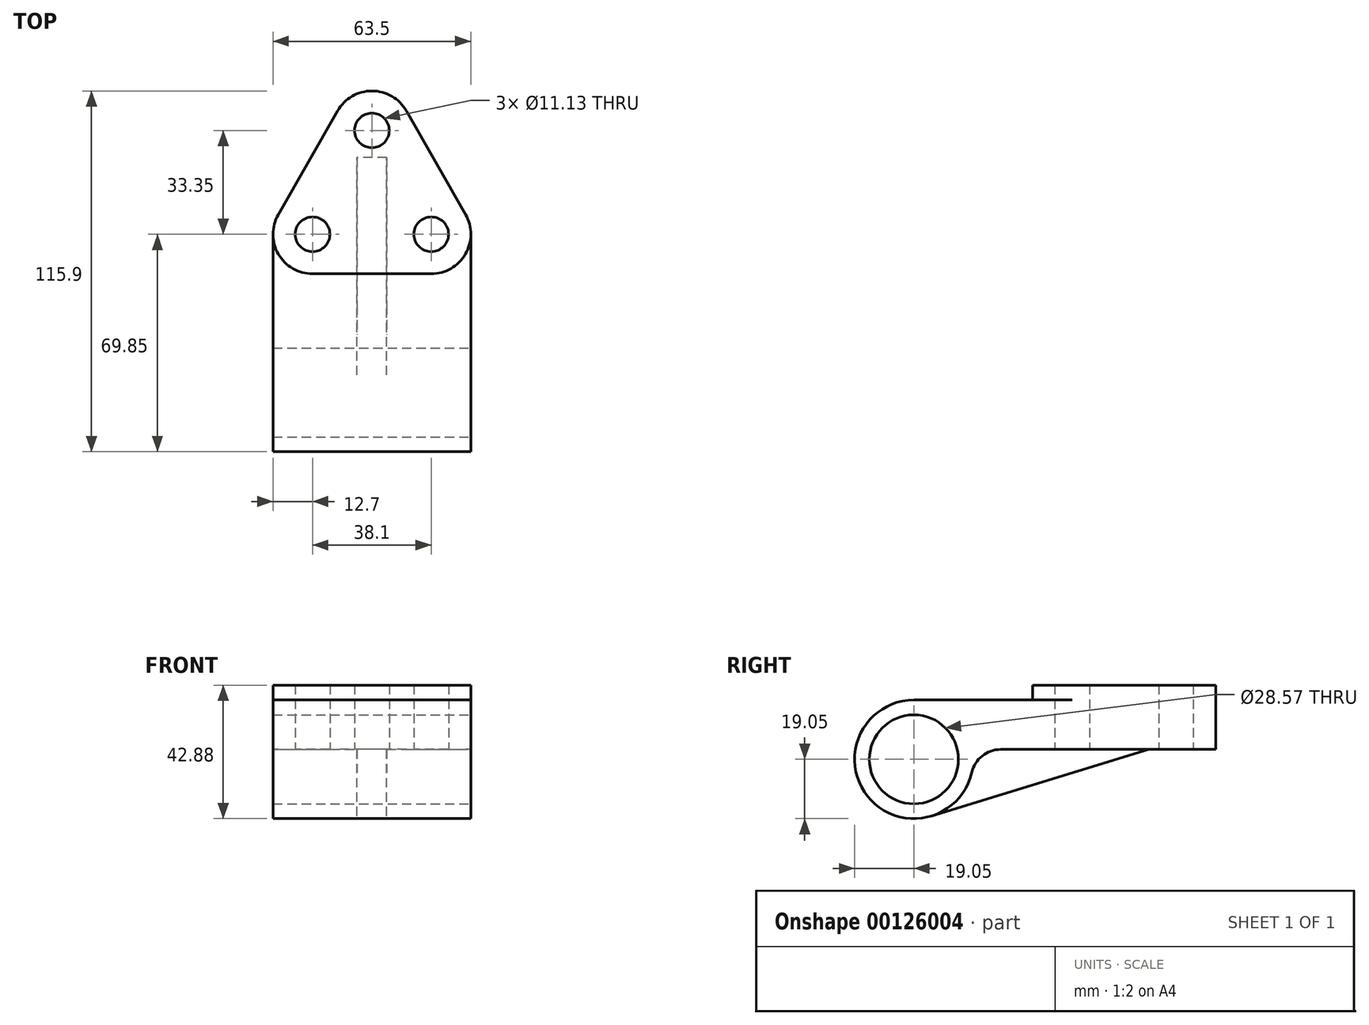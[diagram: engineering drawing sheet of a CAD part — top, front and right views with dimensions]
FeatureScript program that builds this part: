
annotation { "Feature Type Name" : "Feature", "Feature Type Description" : "" }
export const myFeature = defineFeature(function(context is Context, id is Id, definition is map)
    precondition{}
    {
        {
            var Q0;
            Q0=qCreatedBy(makeId("Right.planeOp"),FACE);
            var sketch = newSketch(context, id + "F0", { "sketchPlane" : qUnion([Q0])});
            skArc(sketch, "E0", {"start": v(0, 19.05) * mm, "mid": v(-12.3, -14.55) * mm, "end": v(18.78, 3.17) * mm});
            skCircle(sketch, "E1", {"center": v(0, 0) * mm, "radius": 14.29 * mm});
            skLineSegment(sketch, "E2", {"start": v(0, 19.05) * mm, "end": v(50.8, 19.05) * mm});
            skLineSegment(sketch, "E3", {"start": v(50.8, 19.05) * mm, "end": v(50.8, 3.17) * mm});
            skLineSegment(sketch, "E4", {"start": v(50.8, 3.17) * mm, "end": v(18.78, 3.17) * mm});
            skSolve(sketch);
        }
        {
            var Q0;
            Q0 = qSketchRegion(id + "F0", true);
            extrude(context, id + "F1", {"entities" : qUnion([Q0]), "endBound" : BoundingType.SYMMETRIC, "oppositeDirection" : true, "depth" : 63.5 * mm});
        }
        {
            var Q0;
            Q0=makeQuery(id+"F1.opExtrude","SWEPT_FACE",FACE,{"disambiguationData":[OSD([sQuery(id+"F0.wireOp",EDGE,"E2")])]});
            var sketch = newSketch(context, id + "F2", { "sketchPlane" : qUnion([Q0])});
            skLineSegment(sketch, "E5", {"start": v(0, 50.8) * mm, "end": v(19.05, 50.8) * mm, "construction": true});
            skLineSegment(sketch, "E6", {"start": v(0, 50.8) * mm, "end": v(-19.05, 50.8) * mm, "construction": true});
            skCircle(sketch, "E7", {"center": v(-19.05, 50.8) * mm, "radius": 5.56 * mm});
            skCircle(sketch, "E8", {"center": v(19.05, 50.8) * mm, "radius": 5.56 * mm});
            skArc(sketch, "E9", {"start": v(19.05, 38.1) * mm, "mid": v(30.03, 44.42) * mm, "end": v(30.08, 57.1) * mm});
            skArc(sketch, "E10", {"start": v(-30.08, 57.1) * mm, "mid": v(-30.03, 44.42) * mm, "end": v(-19.05, 38.1) * mm});
            skLineSegment(sketch, "E11", {"start": v(0, 50.8) * mm, "end": v(0, 84.15) * mm, "construction": true});
            skCircle(sketch, "E12", {"center": v(0, 84.15) * mm, "radius": 5.56 * mm});
            skArc(sketch, "E13", {"start": v(11.03, 90.45) * mm, "mid": v(0, 96.85) * mm, "end": v(-11.03, 90.45) * mm});
            skLineSegment(sketch, "E14", {"start": v(-19.05, 38.1) * mm, "end": v(19.05, 38.1) * mm});
            skLineSegment(sketch, "E15", {"start": v(-30.08, 57.1) * mm, "end": v(-11.03, 90.45) * mm});
            skLineSegment(sketch, "E16", {"start": v(11.03, 90.45) * mm, "end": v(30.08, 57.1) * mm});
            skSolve(sketch);
        }
        {
            var Q0;
            Q0 = qSketchRegion(id + "F2", true);
            var Q1;
            Q1=makeQuery(id+"F1.opExtrude","SWEPT_FACE",FACE,{"disambiguationData":[OSD([sQuery(id+"F0.wireOp",EDGE,"E4")])]});
            extrude(context, id + "F3", {"entities" : qUnion([Q0]), "operationType" : NewBodyOperationType.ADD, "depth" : 4.78 * mm, "hasSecondDirection" : true, "secondDirectionBound" : SecondDirectionBoundingType.UP_TO_SURFACE, "secondDirectionOppositeDirection" : true, "secondDirectionBoundEntityFace" : qUnion([Q1]), "secondDirectionDepth" : 25.4 * mm});
        }
        {
            var Q0;
            {var subQ0=sQuery(id+"F2.wireOp",EDGE,"E7");var subQ1=makeQuery(id+"F1.opExtrude","SWEPT_EDGE",EDGE,{"disambiguationData":[OSD([sQuery(id+"F0.wireOp",EDGE,"E2"),sQuery(id+"F0.wireOp",EDGE,"E3")])]});var subQ2=makeQuery(id+"F2.imprint","INTERSECT",VERTEX,{"disambiguationData":[OD(0.0)],"derivedFrom":[subQ1,subQ0]});Q0=makeQuery(id+"F2.imprint","IMPRINT",FACE,{"disambiguationData":[TD([[makeQuery(id+"F2.imprint","IMPRINT",EDGE,{"disambiguationData":[TD([[subQ2,-1.0]])],"derivedFrom":subQ0}),1.0]])]});}
            var Q1;
            {var subQ0=sQuery(id+"F2.wireOp",EDGE,"E8");var subQ1=makeQuery(id+"F1.opExtrude","SWEPT_EDGE",EDGE,{"disambiguationData":[OSD([sQuery(id+"F0.wireOp",EDGE,"E2"),sQuery(id+"F0.wireOp",EDGE,"E3")])]});var subQ2=makeQuery(id+"F2.imprint","INTERSECT",VERTEX,{"disambiguationData":[OD(0.0)],"derivedFrom":[subQ1,subQ0]});Q1=makeQuery(id+"F2.imprint","IMPRINT",FACE,{"disambiguationData":[TD([[makeQuery(id+"F2.imprint","IMPRINT",EDGE,{"disambiguationData":[TD([[subQ2,1.0]])],"derivedFrom":subQ0}),1.0]])]});}
            var Q2;
            {var subQ0=sQuery(id+"F0.wireOp",EDGE,"E4");Q2=makeQuery(id+"F3.boolean.opBoolean","MERGE",FACE,{"derivedFrom":[makeQuery(id+"F1.opExtrude","SWEPT_FACE",FACE,{"disambiguationData":[OSD([subQ0])]}),makeQuery(id+"F3.opExtrude","CAP_FACE",FACE,{"disambiguationData":[OSD([subQ0])],"isStart":true})]});}
            extrude(context, id + "F4", {"entities" : qUnion([Q0, Q1]), "operationType" : NewBodyOperationType.REMOVE, "endBound" : BoundingType.UP_TO_SURFACE, "oppositeDirection" : true, "endBoundEntityFace" : qUnion([Q2]), "depth" : 25.4 * mm});
        }
        {
            var Q0;
            Q0=makeQuery(id+"F1.opExtrude","SWEPT_EDGE",EDGE,{"disambiguationData":[OSD([sQuery(id+"F0.wireOp",EDGE,"E0"),sQuery(id+"F0.wireOp",EDGE,"E4")])]});
            fillet(context, id + "F5", {"entities" : qUnion([Q0]), "radius" : 9.52 * mm, "tangentPropagation" : true, "allowEdgeOverflow" : false});
        }
        {
            var Q0;
            Q0=qCreatedBy(makeId("Right.planeOp"),FACE);
            var sketch = newSketch(context, id + "F6", { "sketchPlane" : qUnion([Q0])});
            skArc(sketch, "E17.0", {"start": v(0, 19.05) * mm, "mid": v(-12.3, -14.55) * mm, "end": v(18.78, 3.17) * mm});
            skLineSegment(sketch, "E18.0", {"start": v(50.8, 3.17) * mm, "end": v(18.78, 3.17) * mm});
            skLineSegment(sketch, "E19", {"start": v(5.58, -18.22) * mm, "end": v(75.43, 3.18) * mm});
            skLineSegment(sketch, "E20", {"start": v(75.43, 3.17) * mm, "end": v(5.58, 3.17) * mm});
            skLineSegment(sketch, "E21", {"start": v(5.58, 3.17) * mm, "end": v(5.58, -18.22) * mm});
            skSolve(sketch);
        }
        {
            var Q0;
            Q0 = qSketchRegion(id + "F6", true);
            extrude(context, id + "F7", {"entities" : qUnion([Q0]), "operationType" : NewBodyOperationType.ADD, "endBound" : BoundingType.SYMMETRIC, "depth" : 9.52 * mm});
        }
        {
            var Q0;
            Q0=makeQuery(id+"F0.imprint","IMPRINT",FACE,{"disambiguationData":[TD([[makeQuery(id+"F0.imprint","IMPRINT",EDGE,{"derivedFrom":sQuery(id+"F0.wireOp",EDGE,"E1")}),1.0]])]});
            var Q1;
            Q1=sQuery(id+"F0.wireOp",EDGE,"E1");
            extrude(context, id + "F8", {"entities" : qUnion([Q0]), "operationType" : NewBodyOperationType.REMOVE, "surfaceEntities" : qUnion([Q1]), "endBound" : BoundingType.SYMMETRIC, "oppositeDirection" : true, "depth" : 25.4 * mm});
        }
    });
